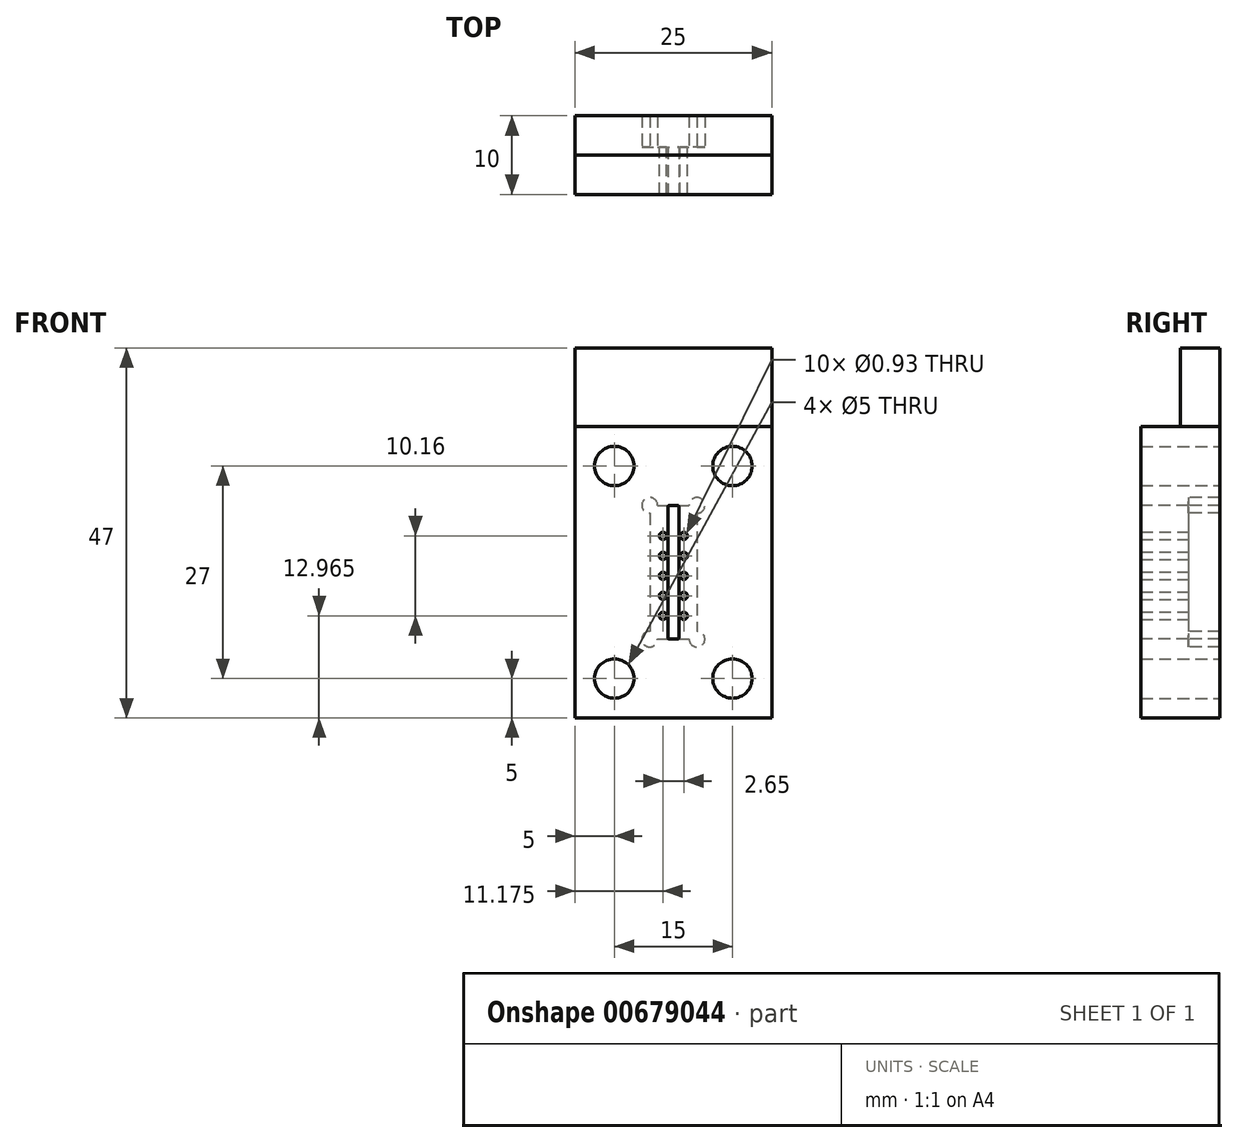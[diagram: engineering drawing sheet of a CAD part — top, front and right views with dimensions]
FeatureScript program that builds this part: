
annotation { "Feature Type Name" : "Feature", "Feature Type Description" : "" }
export const myFeature = defineFeature(function(context is Context, id is Id, definition is map)
    precondition{}
    {
        {
            var Q0;
            Q0=qCreatedBy(makeId("Front.planeOp"),FACE);
            var sketch = newSketch(context, id + "F0", { "sketchPlane" : qUnion([Q0])});
            skLineSegment(sketch, "E0.bottom", {"start": v(0, 0) * mm, "end": v(-25, 0) * mm});
            skLineSegment(sketch, "E0.top", {"start": v(0, 37) * mm, "end": v(-25, 37) * mm});
            skLineSegment(sketch, "E0.left", {"start": v(0, 0) * mm, "end": v(0, 37) * mm});
            skLineSegment(sketch, "E0.right", {"start": v(-25, 0) * mm, "end": v(-25, 37) * mm});
            skLineSegment(sketch, "E1.bottom", {"start": v(-14.5, 27) * mm, "end": v(-10.5, 27) * mm});
            skLineSegment(sketch, "E1.top", {"start": v(-14.5, 10) * mm, "end": v(-10.5, 10) * mm});
            skLineSegment(sketch, "E1.left", {"start": v(-15.5, 26) * mm, "end": v(-15.5, 11) * mm});
            skLineSegment(sketch, "E1.right", {"start": v(-9.5, 26) * mm, "end": v(-9.5, 11) * mm});
            skLineSegment(sketch, "E2.bottom", {"start": v(-13, 27) * mm, "end": v(-12, 27) * mm});
            skLineSegment(sketch, "E2.top", {"start": v(-13, 10) * mm, "end": v(-12, 10) * mm});
            skLineSegment(sketch, "E2.left", {"start": v(-13.2, 26.8) * mm, "end": v(-13.2, 10.2) * mm});
            skLineSegment(sketch, "E2.right", {"start": v(-11.8, 26.8) * mm, "end": v(-11.8, 10.2) * mm});
            skLineSegment(sketch, "E3.bottom", {"start": v(-25, 0) * mm, "end": v(0, 0) * mm});
            skPoint(sketch, "E4.visualSharp", {"position": v(-13.2, 10) * mm});
            skArc(sketch, "E4.filletArc", {"start": v(-13.2, 10.2) * mm, "mid": v(-13.14, 10.06) * mm, "end": v(-13, 10) * mm});
            skPoint(sketch, "E5.visualSharp", {"position": v(-13.2, 27) * mm});
            skArc(sketch, "E5.filletArc", {"start": v(-13, 27) * mm, "mid": v(-13.14, 26.94) * mm, "end": v(-13.2, 26.8) * mm});
            skPoint(sketch, "E6.visualSharp", {"position": v(-11.8, 27) * mm});
            skArc(sketch, "E6.filletArc", {"start": v(-11.8, 26.8) * mm, "mid": v(-11.86, 26.94) * mm, "end": v(-12, 27) * mm});
            skPoint(sketch, "E7.visualSharp", {"position": v(-11.8, 10) * mm});
            skArc(sketch, "E7.filletArc", {"start": v(-12, 10) * mm, "mid": v(-11.86, 10.06) * mm, "end": v(-11.8, 10.2) * mm});
            skArc(sketch, "E8", {"start": v(-9.5, 11) * mm, "mid": v(-8.8, 9.3) * mm, "end": v(-10.5, 10) * mm});
            skArc(sketch, "E9", {"start": v(-9.5, 26) * mm, "mid": v(-8.8, 27.7) * mm, "end": v(-10.5, 27) * mm});
            skArc(sketch, "E10", {"start": v(-14.5, 27) * mm, "mid": v(-16.2, 27.7) * mm, "end": v(-15.5, 26) * mm});
            skArc(sketch, "E11", {"start": v(-14.5, 10) * mm, "mid": v(-16.2, 9.3) * mm, "end": v(-15.5, 11) * mm});
            skSolve(sketch);
        }
        {
            var Q0;
            Q0=makeQuery(id+"F0.imprint","IMPRINT",FACE,{"disambiguationData":[TD([[makeQuery(id+"F0.imprint","IMPRINT",EDGE,{"derivedFrom":sQuery(id+"F0.wireOp",EDGE,"E0.top")}),1.0]])]});
            extrude(context, id + "F1", {"entities" : qUnion([Q0]), "oppositeDirection" : true, "depth" : 10 * mm, "offsetDistance" : 25 * mm});
        }
        {
            var Q0;
            Q0=makeQuery(id+"F0.imprint","IMPRINT",FACE,{"disambiguationData":[TD([[makeQuery(id+"F0.imprint","IMPRINT",EDGE,{"derivedFrom":sQuery(id+"F0.wireOp",EDGE,"E1.left")}),1.0]])]});
            var Q1;
            Q1=makeQuery(id+"F0.imprint","IMPRINT",FACE,{"disambiguationData":[TD([[makeQuery(id+"F0.imprint","IMPRINT",EDGE,{"derivedFrom":sQuery(id+"F0.wireOp",EDGE,"E1.right")}),-1.0]])]});
            extrude(context, id + "F2", {"entities" : qUnion([Q0, Q1]), "operationType" : NewBodyOperationType.ADD, "oppositeDirection" : true, "depth" : 6 * mm, "offsetDistance" : 25 * mm});
        }
        {
            var Q0;
            Q0=makeQuery(id+"F1.opExtrude","CAP_FACE",FACE,{"disambiguationData":[OSD([sQuery(id+"F0.wireOp",EDGE,"E0.top"),sQuery(id+"F0.wireOp",EDGE,"E0.left"),sQuery(id+"F0.wireOp",EDGE,"E0.right"),sQuery(id+"F0.wireOp",EDGE,"E1.bottom"),sQuery(id+"F0.wireOp",EDGE,"E1.top"),sQuery(id+"F0.wireOp",EDGE,"E1.left"),sQuery(id+"F0.wireOp",EDGE,"E1.right"),sQuery(id+"F0.wireOp",EDGE,"E2.bottom"),sQuery(id+"F0.wireOp",EDGE,"E2.top"),sQuery(id+"F0.wireOp",EDGE,"E3.bottom"),sQuery(id+"F0.wireOp",EDGE,"E8"),sQuery(id+"F0.wireOp",EDGE,"E9"),sQuery(id+"F0.wireOp",EDGE,"E10"),sQuery(id+"F0.wireOp",EDGE,"E11")])],"isStart":false});
            var sketch = newSketch(context, id + "F3", { "sketchPlane" : qUnion([Q0])});
            skLineSegment(sketch, "E12.bottom", {"start": v(0, 37) * mm, "end": v(25, 37) * mm});
            skLineSegment(sketch, "E12.top", {"start": v(0, 47) * mm, "end": v(25, 47) * mm});
            skLineSegment(sketch, "E12.left", {"start": v(0, 37) * mm, "end": v(0, 47) * mm});
            skLineSegment(sketch, "E12.right", {"start": v(25, 37) * mm, "end": v(25, 47) * mm});
            skSolve(sketch);
        }
        {
            var Q0;
            Q0 = qSketchRegion(id + "F3", true);
            extrude(context, id + "F4", {"entities" : qUnion([Q0]), "oppositeDirection" : true, "depth" : 5 * mm, "offsetDistance" : 25 * mm});
        }
        {
            var Q0;
            Q0=makeQuery(id+"F2.opExtrude","CAP_FACE",FACE,{"disambiguationData":[OSD([sQuery(id+"F0.wireOp",EDGE,"E1.bottom"),sQuery(id+"F0.wireOp",EDGE,"E1.top"),sQuery(id+"F0.wireOp",EDGE,"E1.left"),sQuery(id+"F0.wireOp",EDGE,"E2.left"),sQuery(id+"F0.wireOp",EDGE,"E4.filletArc"),sQuery(id+"F0.wireOp",EDGE,"E5.filletArc"),sQuery(id+"F0.wireOp",EDGE,"E10"),sQuery(id+"F0.wireOp",EDGE,"E11")])],"isStart":false});
            var sketch = newSketch(context, id + "F5", { "sketchPlane" : qUnion([Q0])});
            skCircle(sketch, "E13", {"center": v(13.83, 12.97) * mm, "radius": 0.47 * mm});
            skCircle(sketch, "E14.0.1.0", {"center": v(13.83, 15.5) * mm, "radius": 0.47 * mm});
            skCircle(sketch, "E14.0.2.0", {"center": v(13.83, 18.05) * mm, "radius": 0.47 * mm});
            skCircle(sketch, "E14.0.3.0", {"center": v(13.83, 20.59) * mm, "radius": 0.47 * mm});
            skCircle(sketch, "E14.0.4.0", {"center": v(13.83, 23.13) * mm, "radius": 0.47 * mm});
            skCircle(sketch, "E14.1.0.0", {"center": v(11.18, 12.97) * mm, "radius": 0.47 * mm});
            skCircle(sketch, "E14.1.1.0", {"center": v(11.18, 15.5) * mm, "radius": 0.47 * mm});
            skCircle(sketch, "E14.1.2.0", {"center": v(11.18, 18.05) * mm, "radius": 0.47 * mm});
            skCircle(sketch, "E14.1.3.0", {"center": v(11.18, 20.59) * mm, "radius": 0.47 * mm});
            skCircle(sketch, "E14.1.4.0", {"center": v(11.18, 23.13) * mm, "radius": 0.47 * mm});
            skLineSegment(sketch, "E14.direction1", {"start": v(13.83, 12.97) * mm, "end": v(11.18, 12.97) * mm, "construction": true});
            skLineSegment(sketch, "E14.direction2", {"start": v(13.83, 12.97) * mm, "end": v(13.83, 15.5) * mm, "construction": true});
            skSolve(sketch);
        }
        {
            var Q0;
            Q0=makeQuery(id+"F5.imprint","IMPRINT",FACE,{"disambiguationData":[TD([[makeQuery(id+"F5.imprint","IMPRINT",EDGE,{"derivedFrom":sQuery(id+"F5.wireOp",EDGE,"E13")}),1.0]])]});
            var Q1;
            Q1=makeQuery(id+"F5.imprint","IMPRINT",FACE,{"disambiguationData":[TD([[makeQuery(id+"F5.imprint","IMPRINT",EDGE,{"derivedFrom":sQuery(id+"F5.wireOp",EDGE,"E14.0.1.0")}),1.0]])]});
            var Q2;
            Q2=makeQuery(id+"F5.imprint","IMPRINT",FACE,{"disambiguationData":[TD([[makeQuery(id+"F5.imprint","IMPRINT",EDGE,{"derivedFrom":sQuery(id+"F5.wireOp",EDGE,"E14.0.2.0")}),1.0]])]});
            var Q3;
            Q3=makeQuery(id+"F5.imprint","IMPRINT",FACE,{"disambiguationData":[TD([[makeQuery(id+"F5.imprint","IMPRINT",EDGE,{"derivedFrom":sQuery(id+"F5.wireOp",EDGE,"E14.0.3.0")}),1.0]])]});
            var Q4;
            Q4=makeQuery(id+"F5.imprint","IMPRINT",FACE,{"disambiguationData":[TD([[makeQuery(id+"F5.imprint","IMPRINT",EDGE,{"derivedFrom":sQuery(id+"F5.wireOp",EDGE,"E14.0.4.0")}),1.0]])]});
            var Q5;
            Q5=makeQuery(id+"F5.imprint","IMPRINT",FACE,{"disambiguationData":[TD([[makeQuery(id+"F5.imprint","IMPRINT",EDGE,{"derivedFrom":sQuery(id+"F5.wireOp",EDGE,"E14.1.4.0")}),1.0]])]});
            var Q6;
            Q6=makeQuery(id+"F5.imprint","IMPRINT",FACE,{"disambiguationData":[TD([[makeQuery(id+"F5.imprint","IMPRINT",EDGE,{"derivedFrom":sQuery(id+"F5.wireOp",EDGE,"E14.1.3.0")}),1.0]])]});
            var Q7;
            Q7=makeQuery(id+"F5.imprint","IMPRINT",FACE,{"disambiguationData":[TD([[makeQuery(id+"F5.imprint","IMPRINT",EDGE,{"derivedFrom":sQuery(id+"F5.wireOp",EDGE,"E14.1.2.0")}),1.0]])]});
            var Q8;
            Q8=makeQuery(id+"F5.imprint","IMPRINT",FACE,{"disambiguationData":[TD([[makeQuery(id+"F5.imprint","IMPRINT",EDGE,{"derivedFrom":sQuery(id+"F5.wireOp",EDGE,"E14.1.1.0")}),1.0]])]});
            var Q9;
            Q9=makeQuery(id+"F5.imprint","IMPRINT",FACE,{"disambiguationData":[TD([[makeQuery(id+"F5.imprint","IMPRINT",EDGE,{"derivedFrom":sQuery(id+"F5.wireOp",EDGE,"E14.1.0.0")}),1.0]])]});
            extrude(context, id + "F6", {"entities" : qUnion([Q0, Q1, Q2, Q3, Q4, Q5, Q6, Q7, Q8, Q9]), "operationType" : NewBodyOperationType.REMOVE, "endBound" : BoundingType.THROUGH_ALL, "oppositeDirection" : true, "depth" : 25 * mm, "offsetDistance" : 25 * mm});
        }
        {
            var Q0;
            Q0=makeQuery(id+"F1.opExtrude","CAP_FACE",FACE,{"disambiguationData":[OSD([sQuery(id+"F0.wireOp",EDGE,"E0.top"),sQuery(id+"F0.wireOp",EDGE,"E0.left"),sQuery(id+"F0.wireOp",EDGE,"E0.right"),sQuery(id+"F0.wireOp",EDGE,"E1.bottom"),sQuery(id+"F0.wireOp",EDGE,"E1.top"),sQuery(id+"F0.wireOp",EDGE,"E1.left"),sQuery(id+"F0.wireOp",EDGE,"E1.right"),sQuery(id+"F0.wireOp",EDGE,"E2.bottom"),sQuery(id+"F0.wireOp",EDGE,"E2.top"),sQuery(id+"F0.wireOp",EDGE,"E3.bottom"),sQuery(id+"F0.wireOp",EDGE,"E8"),sQuery(id+"F0.wireOp",EDGE,"E9"),sQuery(id+"F0.wireOp",EDGE,"E10"),sQuery(id+"F0.wireOp",EDGE,"E11")])],"isStart":false});
            var sketch = newSketch(context, id + "F7", { "sketchPlane" : qUnion([Q0])});
            skCircle(sketch, "E15", {"center": v(5, 32) * mm, "radius": 2.5 * mm});
            skCircle(sketch, "E16.0.1.0", {"center": v(5, 5) * mm, "radius": 2.5 * mm});
            skCircle(sketch, "E16.1.0.0", {"center": v(20, 32) * mm, "radius": 2.5 * mm});
            skCircle(sketch, "E16.1.1.0", {"center": v(20, 5) * mm, "radius": 2.5 * mm});
            skLineSegment(sketch, "E16.direction1", {"start": v(5, 32) * mm, "end": v(20, 32) * mm, "construction": true});
            skLineSegment(sketch, "E16.direction2", {"start": v(5, 32) * mm, "end": v(5, 5) * mm, "construction": true});
            skSolve(sketch);
        }
        {
            var Q0;
            Q0=makeQuery(id+"F7.imprint","IMPRINT",FACE,{"disambiguationData":[TD([[makeQuery(id+"F7.imprint","IMPRINT",EDGE,{"derivedFrom":sQuery(id+"F7.wireOp",EDGE,"E15")}),1.0]])]});
            var Q1;
            Q1=makeQuery(id+"F7.imprint","IMPRINT",FACE,{"disambiguationData":[TD([[makeQuery(id+"F7.imprint","IMPRINT",EDGE,{"derivedFrom":sQuery(id+"F7.wireOp",EDGE,"E16.1.0.0")}),1.0]])]});
            var Q2;
            Q2=makeQuery(id+"F7.imprint","IMPRINT",FACE,{"disambiguationData":[TD([[makeQuery(id+"F7.imprint","IMPRINT",EDGE,{"derivedFrom":sQuery(id+"F7.wireOp",EDGE,"E16.1.1.0")}),1.0]])]});
            var Q3;
            Q3=makeQuery(id+"F7.imprint","IMPRINT",FACE,{"disambiguationData":[TD([[makeQuery(id+"F7.imprint","IMPRINT",EDGE,{"derivedFrom":sQuery(id+"F7.wireOp",EDGE,"E16.0.1.0")}),1.0]])]});
            extrude(context, id + "F8", {"entities" : qUnion([Q0, Q1, Q2, Q3]), "operationType" : NewBodyOperationType.REMOVE, "endBound" : BoundingType.THROUGH_ALL, "oppositeDirection" : true, "depth" : 25 * mm, "offsetDistance" : 25 * mm});
        }
    });
